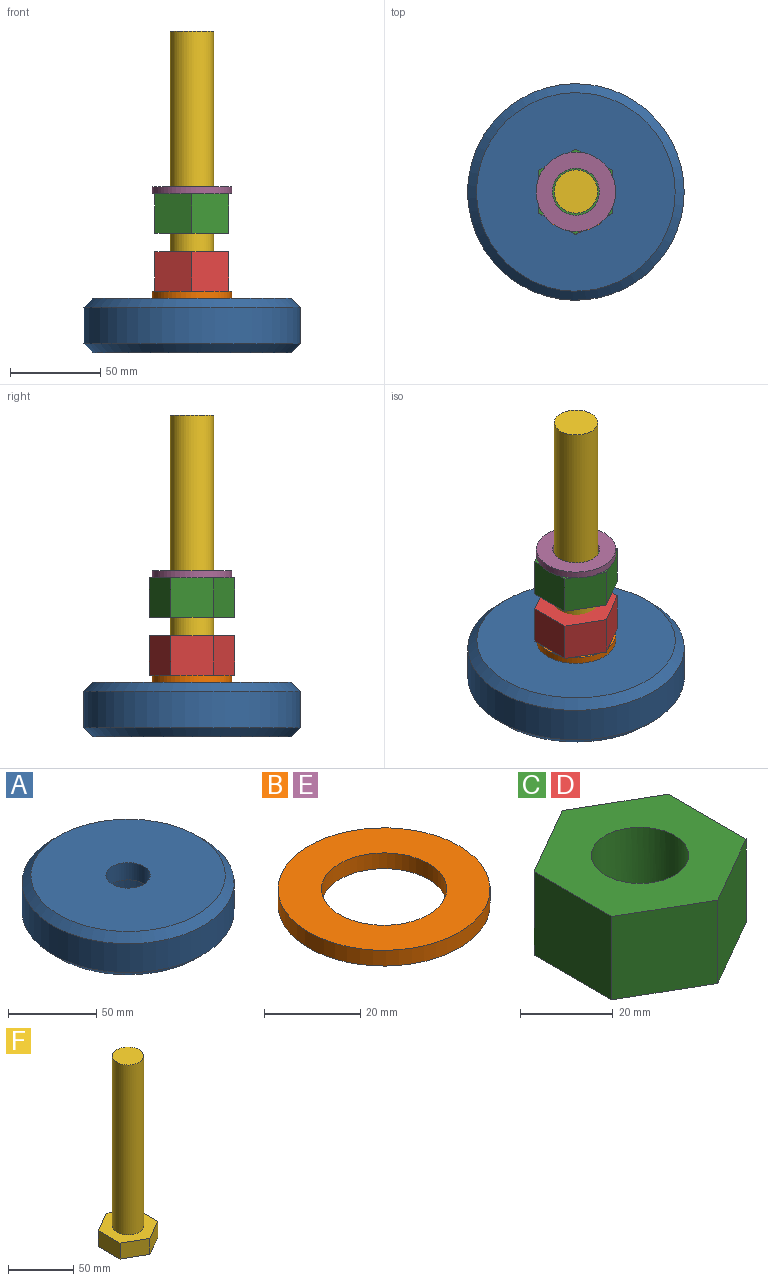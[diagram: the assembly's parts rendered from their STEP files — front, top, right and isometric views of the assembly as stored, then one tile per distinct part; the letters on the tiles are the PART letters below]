
ASSEMBLY  parts=6 mates=5
PART A: 8 faces, bbox 120x120x30 mm
  f0: plane 110x110mm, normal (0,0,-1), area 7127.5mm2, adj f4,f6
  f1: cylinder r=12.5mm len=25mm, axis (0,0,1), area 942.5mm2, adj f3,f5
  f2: cylinder r=60mm len=120mm, axis (0,0,1), area 7539.8mm2, adj f6,f7
  f3: plane 110x110mm, normal (0,0,1), area 9012.4mm2, adj f1,f7
  f4: cylinder r=27.5mm len=55mm, axis (0,0,-1), area 3110.2mm2, adj f0,f5
  f5: plane 55x55mm, normal (0,0,-1), area 1885mm2, adj f1,f4
  f6: cone r=60mm half-angle=45deg, axis (0,0,1), area 2554.7mm2, adj f0,f2
  f7: cone r=55mm half-angle=45deg, axis (0,0,-1), area 2554.7mm2, adj f2,f3
PART B: 4 faces, bbox 44x44x4 mm
  f0: cylinder r=13mm len=26mm, axis (0,0,-1), area 326.7mm2, adj f2,f3
  f1: cylinder r=22mm len=44mm, axis (0,0,-1), area 552.9mm2, adj f2,f3
  f2: plane 44x44mm, normal (0,0,1), area 989.6mm2, adj f0,f1
  f3: plane 44x44mm, normal (0,0,-1), area 989.6mm2, adj f0,f1
PART C: 9 faces, bbox 41x47.3x22 mm
  f0: plane 22x20.5mm, normal (0.5,0.87,0), area 520.8mm2, adj f1,f5,f6,f7
  f1: plane 22x20.5mm, normal (-0.5,0.87,0), area 520.8mm2, adj f0,f2,f6,f7
  f2: plane 23.67x22mm, normal (-1,0,0), area 520.8mm2, adj f1,f3,f6,f7
  f3: plane 22x20.5mm, normal (-0.5,-0.87,0), area 520.8mm2, adj f2,f4,f6,f7
  f4: plane 22x20.5mm, normal (0.5,-0.87,0), area 520.8mm2, adj f3,f5,f6,f7
  f5: plane 23.67x22mm, normal (1,0,0), area 520.8mm2, adj f0,f4,f6,f7
  f6: plane 47.34x41mm, normal (0,0,1), area 1109.4mm2, adj f0,f1,f2,f3,f4,f5,f8
  f7: plane 47.34x41mm, normal (0,0,-1), area 1109.4mm2, adj f0,f1,f2,f3,f4,f5,f8
  f8: cylinder r=10.5mm len=22mm, axis (0,0,-1), area 1451.4mm2, adj f6,f7
PART D: same geometry as C
PART E: same geometry as B
PART F: 10 faces, bbox 41x47.3x175 mm
  f0: plane 20.5x15mm, normal (0.5,0.87,0), area 355.1mm2, adj f1,f5,f6,f7
  f1: plane 20.5x15mm, normal (-0.5,0.87,0), area 355.1mm2, adj f0,f2,f6,f7
  f2: plane 23.67x15mm, normal (-1,0,0), area 355.1mm2, adj f1,f3,f6,f7
  f3: plane 20.5x15mm, normal (-0.5,-0.87,0), area 355.1mm2, adj f2,f4,f6,f7
  f4: plane 20.5x15mm, normal (0.5,-0.87,0), area 355.1mm2, adj f3,f5,f6,f7
  f5: plane 23.67x15mm, normal (1,0,0), area 355.1mm2, adj f0,f4,f6,f7
  f6: plane 47.34x41mm, normal (0,0,1), area 1003.4mm2, adj f0,f1,f2,f3,f4,f5,f8
  f7: plane 47.34x41mm, normal (0,0,-1), area 1455.8mm2, adj f0,f1,f2,f3,f4,f5
  f8: cylinder r=12mm len=160mm, axis (0,0,-1), area 12063.7mm2, adj f6,f9
  f9: plane 24x24mm, normal (0,0,1), area 452.4mm2, adj f8
PLACE A t=(-54.6,26.74,28.64)mm fixed
PLACE B rot(axis=(1,0,0),180deg) t=(-54.6,146.74,82.64)mm
PLACE C rot(axis=(1,0,0),180deg) t=(-54.6,-93.26,136.64)mm
PLACE D rot(axis=(1,0,0),180deg) t=(-54.6,-93.26,104.64)mm
PLACE E t=(-54.6,-93.26,36.64)mm
PLACE F rot(axis=(0,0,-1),125.5deg) t=(-54.6,26.74,-48.36)mm
MATE fastened B.f0 <-> A.f1  axis (0,0,-1) through (-54.6,26.74,28.64)mm
MATE fastened E.f0 <-> C.f8  axis (0,0,-1) through (-54.6,26.74,86.64)mm
MATE fastened C.f8 <-> D.f8  axis (0,0,-1) through (-54.6,26.74,64.64)mm
MATE revolute F.f8 <-> A.f1  axis (0,0,-1) through (-54.6,26.74,16.64)mm
MATE fastened D.f8 <-> B.f0  axis (0,0,-1) through (-54.6,26.74,32.64)mm
